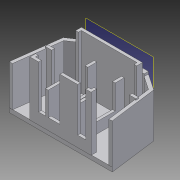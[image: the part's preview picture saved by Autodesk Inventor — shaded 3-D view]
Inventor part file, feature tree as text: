
AUTODESK INVENTOR PART (.ipt)
format: ipt  version: 2012 (Build 160160000, 160)  size: 264,704 bytes
history: native  units: mm
features: extrude x10, sketch x10, plane x1
ambient origin geometry x8: Origin, YZ Plane, XZ Plane, XY Plane, X Axis, Y Axis, Z Axis, Center Point
bodies: Volumenkörper1 (feature_tree)
feature tree (21):
  extrude  "Extrusion1"  Depth=28.5mm
  extrude  "Extrusion2"  Depth=25.5mm TaperAngle=0.0deg
  extrude  "Extrusion3"  Depth=1.25mm
  extrude  "Extrusion4"  Depth=6.0mm
  extrude  "Extrusion5"  Depth=16.35mm TaperAngle=0.0deg
  extrude  "Extrusion6"  Depth=5.0mm TaperAngle=0.0deg
  extrude  "Extrusion7"  Depth=6.25mm
  plane  "Arbeitsebene1"
  extrude  "Extrusion9"  Depth=16.35mm TaperAngle=0.0deg
  extrude  "Extrusion10"  Depth=8.25mm
  extrude  "Extrusion11"  Depth=10.0mm
  sketch  "Skizze1"  dims[d0=26.0mm d1=28.5mm]
  sketch  "Skizze2"  dims[d2=1.25mm d3=25.5mm d4=0.0mm]
  sketch  "Skizze3"  dims[d5=11.5mm d6=1.25mm]
  sketch  "Skizze4"  dims[d7=1.25mm d8=6.0mm]
  sketch  "Skizze5"  dims[d9=6.0mm d10=16.35mm d11=0.0mm]
  sketch  "Skizze6"  dims[d12=12.25mm d13=5.0mm d14=0.0mm]
  sketch  "Skizze7"  dims[d15=12.25mm d16=6.25mm]
  sketch  "Skizze9"  dims[d17=6.25mm d18=16.35mm d19=0.0mm]
  sketch  "Skizze11"  dims[d20=5.25mm d21=8.25mm]
  sketch  "Skizze12"  dims[d22=3.8mm d23=10.0mm d24=4.0mm d25=2.45mm d26=1.3mm d27=0.0mm d28=1.25mm d30=1.25mm d31=1.3mm d32=0.0mm d33=1.3mm d37=2.7mm d38=2.7mm d39=0.0mm d40=3.9mm d41=3.9mm d42=1.3mm d43=3.0mm d44=3.0mm d45=1.3mm d46=19.3mm d47=0.0mm d48=3.5mm d55=27.0mm d56=19.8mm d57=0.75mm d58=0.75mm d59=2.0mm d60=0.0mm d65=28.5mm d66=8.25mm d67=8.25mm d68=6.0mm d69=6.0mm d70=5.5mm d71=5.5mm d72=18.7mm d73=0.0mm d74=2.0mm d75=0.0mm]
